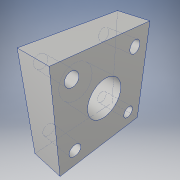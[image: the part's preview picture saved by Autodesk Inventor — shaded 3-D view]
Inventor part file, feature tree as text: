
AUTODESK INVENTOR PART (.ipt)
format: ipt  version: 2019 (Build 230136000, 136)  size: 114,176 bytes
history: native  units: in
note: dims shown in document units (in); Inventor stores cm internally (conversion verified against a paired STEP export)
features: extrude x1, sketch x1
ambient origin geometry x8: Origin, YZ Plane, XZ Plane, XY Plane, X Axis, Y Axis, Z Axis, Center Point
bodies: Solid1 (feature_tree)
feature tree (2):
  extrude  "Extrusion1"  Depth=0.5in
  sketch  "Sketch1"  dims[d0=1.5in d1=0.5781in d2=0.19in d3=1.0in d4=0.5in d5=0.0in]
